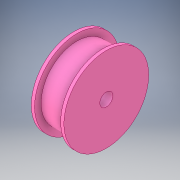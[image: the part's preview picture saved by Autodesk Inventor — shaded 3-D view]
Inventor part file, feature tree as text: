
AUTODESK INVENTOR PART (.ipt)
format: ipt  version: 2017 SP1 (Build 210196100, 196)  size: 133,632 bytes
history: native  units: in
note: dims shown in document units (in); Inventor stores cm internally (conversion verified against a paired STEP export)
features: extrude x4, sketch x4
ambient origin geometry x8: Origin, YZ Plane, XZ Plane, XY Plane, X Axis, Y Axis, Z Axis, Center Point
bodies: Solid1 (feature_tree)
feature tree (8):
  extrude  "Extrusion1"  Depth=0.25in
  extrude  "Extrusion2"  Depth=0.125in
  extrude  "Extrusion3"  Depth=0.0625in TaperAngle=0.0deg
  extrude  "Extrusion4"  Depth=0.375in TaperAngle=0.0deg
  sketch  "Sketch1"  dims[d0=1.375in d2=0.25in]
  sketch  "Sketch2"  dims[d4=0.5in d5=0.0in d6=0.125in]
  sketch  "Sketch3"  dims[d7=0.0625in d8=0.0in d9=0.0625in d10=0.0in]
  sketch  "Sketch4"  dims[d11=0.1875in d12=0.375in d13=0.0in]
